FCSTD DOCUMENT  (FreeCAD 1.0R39109 (Git))
Label: TriggerAssembly
License: All rights reserved
LicenseURL: http://en.wikipedia.org/wiki/All_rights_reserved
objects: App::Link×5, App::FeaturePython×5, Assembly::JointGroup×1, Assembly::AssemblyObject×1
EXTERNAL_REF file=TriggerPivotBusing.stl.FCStd obj=Part
EXTERNAL_REF file=Trigger.stl.FCStd obj=Part001
EXTERNAL_REF file=../../ReferenceParts/M3.FCStd obj=Part

FEATURE [App::Link] Link014  label="TriggerPivotBushing"
  LinkPlacement = pos=(0,7e-16,3) rot=(-1,0,0;3.14159rad)
  LinkedObject = -> <external TriggerPivotBusing.stl.FCStd>#Part
  Placement = pos=(0,7e-16,3) rot=(-1,0,0;3.14159rad)
FEATURE [App::Link] Trigger_stl  label="Trigger.stl"
  LinkedObject = -> <external Trigger.stl.FCStd>#Part001
FEATURE [App::FeaturePython] GroundedJoint  # Assembly grounded joint (typed FeaturePython)
  ObjectToGround = -> Trigger_stl
FEATURE [App::FeaturePython] Joint  label="Fixed"  # Assembly joint (typed FeaturePython)
  Activated = true
  AngleMax = 0
  AngleMin = 0
  Detach1 = false
  Detach2 = false
  Distance = 0
  Distance2 = 0
  EnableAngleMax = false
  EnableAngleMin = false
  EnableLengthMax = false
  EnableLengthMin = false
  JointType = 0 (Fixed)
  LengthMax = 0
  LengthMin = 0
  Placement1 = pos=(0,3e-16,1.5) rot=(0,0,1;3.14159rad)
  Placement2 = pos=(0,3e-16,1.5) rot=(0,1,0;3.14159rad)
  Reference1 = -> Assembly [Link014.Body.Edge3,Link014.Body.Edge3]
  Reference2 = -> Assembly [Trigger_stl.Body.Edge63,Trigger_stl.Body.Edge63]
FEATURE [App::Link] M3x10  label="M3x011"
  LinkPlacement = pos=(-10.3581,0.779318,2.07e-14) rot=(0.970288,-0.171088,-0.171088;1.60095rad)
  LinkedObject = -> <external ../../ReferenceParts/M3.FCStd>#Part
  Placement = pos=(-10.3581,0.779318,2.07e-14) rot=(0.970288,-0.171088,-0.171088;1.60095rad)
FEATURE [App::Link] M3x011  label="M3x012"
  LinkPlacement = pos=(-18,2.55146,-6e-16) rot=(1,0,0;1.5708rad)
  LinkedObject = -> <external ../../ReferenceParts/M3.FCStd>#Part
  Placement = pos=(-18,2.55146,-6e-16) rot=(1,0,0;1.5708rad)
FEATURE [App::Link] M3x012  label="M3x013"
  LinkPlacement = pos=(25,-4,9e-16) rot=(1,0,0;1.5708rad)
  LinkedObject = -> <external ../../ReferenceParts/M3.FCStd>#Part
  Placement = pos=(25,-4,9e-16) rot=(1,0,0;1.5708rad)
FEATURE [App::FeaturePython] Joint002  label="Fixed002"  # Assembly joint (typed FeaturePython)
  Activated = true
  AngleMax = 0
  AngleMin = 0
  Detach1 = false
  Detach2 = false
  Distance = 0
  Distance2 = 0
  EnableAngleMax = false
  EnableAngleMin = false
  EnableLengthMax = false
  EnableLengthMin = false
  JointType = 0 (Fixed)
  LengthMax = 0
  LengthMin = 0
  Offset2 = pos=(0,0,6) rot=(0,0,1;0rad)
  Placement2 = pos=(-10.3581,0.779318,2.07e-14) rot=(0.970288,-0.171088,-0.171088;1.60095rad)
  Reference1 = -> Assembly [M3x10.Screw.Edge30,M3x10.Screw.Edge30]
  Reference2 = -> Assembly [Trigger_stl.Body.Edge30,Trigger_stl.Body.Edge30]
FEATURE [App::FeaturePython] Joint003  label="Fixed003"  # Assembly joint (typed FeaturePython)
  Activated = true
  AngleMax = 0
  AngleMin = 0
  Detach1 = false
  Detach2 = false
  Distance = 0
  Distance2 = 0
  EnableAngleMax = false
  EnableAngleMin = false
  EnableLengthMax = false
  EnableLengthMin = false
  JointType = 0 (Fixed)
  LengthMax = 0
  LengthMin = 0
  Offset2 = pos=(0,0,6) rot=(0,0,1;0rad)
  Placement2 = pos=(-18,2.55146,-6e-16) rot=(1,0,0;1.5708rad)
  Reference1 = -> Assembly [M3x011.Screw.Edge30,M3x011.Screw.Edge30]
  Reference2 = -> Assembly [Trigger_stl.Body.Edge5,Trigger_stl.Body.Edge5]
FEATURE [App::FeaturePython] Joint004  label="Fixed004"  # Assembly joint (typed FeaturePython)
  Activated = true
  AngleMax = 0
  AngleMin = 0
  Detach1 = false
  Detach2 = false
  Distance = 0
  Distance2 = 0
  EnableAngleMax = false
  EnableAngleMin = false
  EnableLengthMax = false
  EnableLengthMin = false
  JointType = 0 (Fixed)
  LengthMax = 0
  LengthMin = 0
  Offset2 = pos=(0,0,6) rot=(0,0,1;0rad)
  Placement2 = pos=(25,-4,9e-16) rot=(1,0,0;1.5708rad)
  Reference1 = -> Assembly [M3x012.Screw.Edge30,M3x012.Screw.Edge30]
  Reference2 = -> Assembly [Trigger_stl.Body.Edge40,Trigger_stl.Body.Edge40]
FEATURE [Assembly::JointGroup] Joints
  Group = -> [GroundedJoint,Joint,Joint002,Joint003,Joint004]
FEATURE [Assembly::AssemblyObject] Assembly  label="TriggerAssembly"
  Group = -> [Joints,Link014,Trigger_stl,GroundedJoint,Joint,M3x10,M3x011,M3x012,Joint002,Joint003,Joint004]
  Origin = -> Origin007
  Type = Assembly

RESOLVED EXTERNAL PARTS (link-assembly join: the EXTERNAL_REF files above that resolve inside this repo's crawl, each included once):
---- part Trigger.stl.FCStd = doc fcstd_24fa011b4839 ----
FCSTD DOCUMENT  (FreeCAD 1.0R39109 (Git))
Label: Trigger.stl
License: All rights reserved
LicenseURL: http://en.wikipedia.org/wiki/All_rights_reserved
objects: Sketcher::SketchObject×5, PartDesign::Pad×2, PartDesign::Pocket×2, PartDesign::Groove×1, PartDesign::Body×1, App::Part×1
note: 26 computed .brp shape members not serialized (recipe doc carries the construction recipe); baked Part::Feature solids carry a one-line shape summary decoded from their .brp

FEATURE [Sketcher::SketchObject] Sketch
  ArcFitTolerance = 1e-06
  AttachmentSupport = -> [XY_Plane002]
  FullyConstrained = true
  MakeInternals = false
  MapMode = 5
  sketch-geometry (17):
    g0: Circle [constr] CenterX=0 CenterY=0 CenterZ=0 NormalX=0 NormalY=0 NormalZ=1 AngleXU=0 Radius=6
    g1: LineSegment [constr] StartX=-5.63816 StartY=2.05212 StartZ=0 EndX=-18 EndY=6.55146 EndZ=0
    g2: LineSegment StartX=5.65685 StartY=2 StartZ=0 EndX=29 EndY=2 EndZ=0
    g3: LineSegment StartX=29 StartY=-2 StartZ=0 EndX=5.65685 EndY=-2 EndZ=0
    g4: LineSegment [constr] StartX=6 StartY=4.5e-15 StartZ=0 EndX=25 EndY=0 EndZ=0
    g5: ArcOfCircle CenterX=0 CenterY=0 CenterZ=0 NormalX=0 NormalY=0 NormalZ=1 AngleXU=0 Radius=6 StartAngle=0.339837 EndAngle=2.23203
    g6: ArcOfCircle CenterX=0 CenterY=0 CenterZ=0 NormalX=0 NormalY=0 NormalZ=1 AngleXU=0 Radius=6 StartAngle=2.928 EndAngle=5.94335
    g7: LineSegment [constr] StartX=-8.90908 StartY=6.63697 StartZ=0 EndX=-10.2772 EndY=2.8782 EndZ=0
    g8: LineSegment [constr] StartX=-18 StartY=8.55146 StartZ=0 EndX=-18 EndY=4.55146 EndZ=0
    g9: GeomPoint [constr] X=-10 Y=3.6397 Z=0
    g10: LineSegment StartX=-23 StartY=4.55146 StartZ=0 EndX=-14 EndY=4.55146 EndZ=0
    g11: LineSegment StartX=-14 StartY=4.55146 StartZ=0 EndX=-14 EndY=4.23321 EndZ=0
    g12: LineSegment StartX=-14 StartY=4.23321 StartZ=0 EndX=-5.86366 EndY=1.27182 EndZ=0
    g13: LineSegment StartX=-21.8309 StartY=8.55146 StartZ=0 EndX=-14.1691 EndY=8.55146 EndZ=0
    g14: LineSegment StartX=-14.1691 StartY=8.55146 StartZ=0 EndX=-3.68456 EndY=4.7354 EndZ=0
    g15: ArcOfCircle CenterX=0 CenterY=0 CenterZ=0 NormalX=0 NormalY=0 NormalZ=1 AngleXU=0 Radius=23.446 StartAngle=2.76825 EndAngle=2.94623
    g16: ArcOfCircle CenterX=0 CenterY=0 CenterZ=0 NormalX=0 NormalY=0 NormalZ=1 AngleXU=0 Radius=29.0689 StartAngle=6.21433 EndAngle=6.35204
  constraints (51):
    c: Coincident(g0,g-1)
    c: Diameter(g0) = 12
    c: PointOnObject(g5,g0)
    c: PointOnObject(g6,g0)
    c: PointOnObject(g1,g0)
    c: PointOnObject(g0,g1)
    c: Angle(g1,g-1) = 0.349066
    c: Horizontal(g2)
    c: Horizontal(g3)
    c: PointOnObject(g4,g0)
    c: PointOnObject(g4,g-1)
    c: Symmetric(g3,g2,g4)
    c: Coincident(g5,g0)
    c: Coincident(g5,g2)
    c: Coincident(g6,g3)
    c: Coincident(g6,g0)
    c: DistanceX(g-1,g4) = 25
    c: Symmetric(g8,g8,g1)
    c: Vertical(g8)
    c: Equal(g7,g8)
    c: DistanceY(g8,g8) = 4
    c: PointOnObject(g9,g1)
    c: DistanceX(g1,g-1) = 18
    c: DistanceX(g9,g-1) = 10
    c: Horizontal(g10)
    c: Coincident(g11,g10)
    c: Coincident(g12,g11)
    c: Coincident(g12,g6)
    c: PointOnObject(g7,g12)
    c: Vertical(g11)
    c: PointOnObject(g8,g10)
    c: DistanceX(g10,g8) = 5
    c: Horizontal(g13)
    c: Symmetric(g13,g13,g8)
    c: Coincident(g14,g13)
    c: Parallel(g14,g1)
    c: Perpendicular(g7,g12)
    c: Coincident(g14,g5)
    c: Perpendicular(g1,g7)
    c: PointOnObject(g9,g7)
    c: DistanceX(g8,g10) = 4
    c: PointOnObject(g7,g14)
    c: Coincident(g15,g0)
    c: Coincident(g15,g13)
    c: Coincident(g15,g10)
    c: Distance(g13,g-1) = 23.446
    c: Distance(g2,g3) = 4
    c: Coincident(g16,g0)
    c: Coincident(g16,g2)
    c: Coincident(g16,g3)
    c: DistanceX(g4,g2) = 4
FEATURE [PartDesign::Pad] Pad
  Direction = (0,0,1)
  Length = 8
  Length2 = 10
  Midplane = true
  Profile = -> Sketch
  ReferenceAxis = -> Sketch [N_Axis]
  Refine = true
  Suppressed = false
  Type = 0
FEATURE [Sketcher::SketchObject] Sketch001
  ArcFitTolerance = 1e-06
  AttachmentOffset = pos=(0,0,0) rot=(0,0,1;-0.174533rad)
  AttachmentSupport = -> [XY_Plane002]
  FullyConstrained = true
  MakeInternals = false
  MapMode = 5
  Placement = pos=(0,0,0) rot=(0,0,1;6.10865rad)
  sketch-geometry (9):
    g0: ArcOfCircle CenterX=58 CenterY=-24 CenterZ=0 NormalX=0 NormalY=0 NormalZ=1 AngleXU=0 Radius=59 StartAngle=2.82598 EndAngle=3.32291
    g1: ArcOfCircle CenterX=-2 CenterY=-35 CenterZ=0 NormalX=0 NormalY=0 NormalZ=1 AngleXU=0 Radius=2 StartAngle=3.38066 EndAngle=6.46451
    g2: ArcOfCircle CenterX=87.924 CenterY=-13.0833 CenterZ=0 NormalX=0 NormalY=0 NormalZ=1 AngleXU=0 Radius=94.5563 StartAngle=3.01546 EndAngle=3.38066
    g3: GeomPoint X=0 Y=-35 Z=0
    g4: Circle [constr] CenterX=0 CenterY=0 CenterZ=0 NormalX=0 NormalY=0 NormalZ=1 AngleXU=0 Radius=6
    g5: ArcOfCircle CenterX=0 CenterY=0 CenterZ=0 NormalX=0 NormalY=0 NormalZ=1 AngleXU=0 Radius=6 StartAngle=3.34098 EndAngle=5.0371
    g6: GeomPoint X=-1 Y=-24 Z=0
    g7: GeomPoint X=0 Y=-24 Z=0
    g8: GeomPoint X=-6 Y=-24 Z=0
  constraints (23):
    c: Tangent(g2,g1) = -1.5708
    c: Tangent(g1,g0) = 1.5708
    c: PointOnObject(g3,g1)
    c: Horizontal(g3,g1)
    c: DistanceY(g3,g-1) = 35
    c: Radius(g1) = 2
    c: Coincident(g4,g-1)
    c: Diameter(g4) = 12
    c: Coincident(g5,g4)
    c: Coincident(g5,g0)
    c: Coincident(g5,g2)
    c: PointOnObject(g3,g-2)
    c: PointOnObject(g0,g4)
    c: PointOnObject(g6,g0)
    c: PointOnObject(g7,g-2)
    c: Horizontal(g7,g6)
    c: DistanceX(g6,g7) = 1
    c: Horizontal(g0,g7)
    c: PointOnObject(g8,g2)
    c: Horizontal(g8,g6)
    c: DistanceX(g8,g6) = 5
    c: Distance(g2,g0) = 9
    c: DistanceY(g7,g-1) = 24
FEATURE [PartDesign::Pad] Pad001
  BaseFeature = -> Pad
  Direction = (0,0,1)
  Length = 8
  Length2 = 10
  Midplane = true
  Profile = -> Sketch001
  ReferenceAxis = -> Sketch001 [N_Axis]
  Refine = true
  Suppressed = false
  Type = 0
FEATURE [Sketcher::SketchObject] Sketch002
  ArcFitTolerance = 1e-06
  AttachmentSupport = -> [XZ_Plane002]
  FullyConstrained = true
  MakeInternals = false
  MapMode = 5
  Placement = pos=(0,0,0) rot=(1,0,0;1.5708rad)
  sketch-geometry (6):
    g0: LineSegment StartX=0 StartY=-20 StartZ=0 EndX=-4.1 EndY=-20 EndZ=0
    g1: LineSegment StartX=-4.1 StartY=-20 StartZ=0 EndX=-4.1 EndY=1.5 EndZ=0
    g2: LineSegment StartX=-4.1 StartY=1.5 StartZ=0 EndX=-6 EndY=1.5 EndZ=0
    g3: LineSegment StartX=-6 StartY=1.5 StartZ=0 EndX=-24.5 EndY=20 EndZ=0
    g4: LineSegment StartX=-24.5 StartY=20 StartZ=0 EndX=0 EndY=20 EndZ=0
    g5: LineSegment StartX=0 StartY=20 StartZ=0 EndX=0 EndY=-20 EndZ=0
  constraints (18):
    c: PointOnObject(g0,g-2)
    c: Horizontal(g0)
    c: Coincident(g0,g1)
    c: Vertical(g1)
    c: Coincident(g1,g2)
    c: Horizontal(g2)
    c: Coincident(g2,g3)
    c: Coincident(g3,g4)
    c: Horizontal(g4)
    c: Coincident(g4,g5)
    c: Coincident(g5,g0)
    c: Vertical(g5)
    c: DistanceY(g0,g-1) = 20
    c: DistanceX(g0,g-1) = 4.1
    c: DistanceX(g2,g-1) = 6
    c: DistanceY(g-1,g1) = 1.5
    c: Angle(g2,g3) = 2.35619
    c: DistanceY(g-1,g4) = 20
FEATURE [PartDesign::Groove] Groove
  Angle = 360
  Angle2 = 60
  Axis = (0,2e-16,1)
  Base = (0,0,0)
  BaseFeature = -> Pad001
  Profile = -> Sketch002
  ReferenceAxis = -> Sketch002 [V_Axis]
  Refine = true
  Reversed = true
  Suppressed = false
  Type = 0
FEATURE [Sketcher::SketchObject] Sketch003
  ArcFitTolerance = 1e-06
  AttachmentSupport = -> [XZ_Plane002]
  FullyConstrained = true
  MakeInternals = false
  MapMode = 5
  Placement = pos=(0,0,0) rot=(1,0,0;1.5708rad)
  sketch-geometry (2):
    g0: Circle CenterX=25 CenterY=0 CenterZ=0 NormalX=0 NormalY=0 NormalZ=1 AngleXU=0 Radius=1.25
    g1: Circle CenterX=-18 CenterY=0 CenterZ=0 NormalX=0 NormalY=0 NormalZ=1 AngleXU=0 Radius=1.25
  constraints (6):
    c: PointOnObject(g0,g-1)
    c: PointOnObject(g1,g-1)
    c: DistanceX(g1,g-1) = 18
    c: DistanceX(g-1,g0) = 25
    c: Equal(g0,g1)
    c: Diameter(g1) = 2.5
FEATURE [PartDesign::Pocket] Pocket  label="BoltHoles1"
  BaseFeature = -> Groove
  Direction = (0,1,-2e-16)
  Length = 5
  Length2 = 5
  Midplane = true
  Profile = -> Sketch003
  ReferenceAxis = -> Sketch003 [N_Axis]
  Refine = true
  Suppressed = false
  Type = 1
FEATURE [Sketcher::SketchObject] Sketch004
  ArcFitTolerance = 1e-06
  AttachmentOffset = pos=(0,0,0) rot=(0,-1,0;0.349066rad)
  AttachmentSupport = -> [XZ_Plane002]
  FullyConstrained = true
  MakeInternals = false
  MapMode = 5
  Placement = pos=(0,0,0) rot=(0.970288,-0.171088,-0.171088;1.60095rad)
  sketch-geometry (1):
    g0: Circle CenterX=-10 CenterY=0 CenterZ=0 NormalX=0 NormalY=0 NormalZ=1 AngleXU=0 Radius=1.25
  constraints (3):
    c: PointOnObject(g0,g-1)
    c: DistanceX(g0,g-1) = 10
    c: Diameter(g0) = 2.5
FEATURE [PartDesign::Pocket] Pocket001
  BaseFeature = -> Pocket
  Direction = (0.34202,0.939693,-1e-16)
  Length = 5
  Length2 = 5
  Midplane = true
  Profile = -> Sketch004
  ReferenceAxis = -> Sketch004 [N_Axis]
  Refine = true
  Suppressed = false
  Type = 1
FEATURE [PartDesign::Body] Body
  AllowCompound = false
  Group = -> [Sketch,Pad,Sketch001,Pad001,Sketch002,Groove,Sketch003,Pocket,Sketch004,Pocket001]
  Origin = -> Origin002
  Tip = -> Pocket001
FEATURE [App::Part] Part001  label="Trigger.stl"
  Group = -> [Body]
  Origin = -> Origin001
---- part TriggerPivotBusing.stl.FCStd = doc fcstd_a534dfd0ede6 ----
FCSTD DOCUMENT  (FreeCAD 1.0R39109 (Git))
Label: TriggerPivotBusing.stl
License: All rights reserved
LicenseURL: http://en.wikipedia.org/wiki/All_rights_reserved
objects: Sketcher::SketchObject×1, PartDesign::Revolution×1, PartDesign::Chamfer×1, PartDesign::Body×1, App::Part×1
note: 9 computed .brp shape members not serialized (recipe doc carries the construction recipe); baked Part::Feature solids carry a one-line shape summary decoded from their .brp

FEATURE [Sketcher::SketchObject] Sketch
  ArcFitTolerance = 1e-06
  AttachmentSupport = -> [XZ_Plane]
  FullyConstrained = true
  MakeInternals = false
  MapMode = 5
  Placement = pos=(0,0,0) rot=(1,0,0;1.5708rad)
  sketch-geometry (9):
    g0: LineSegment StartX=-1.6 StartY=0 StartZ=0 EndX=-6 EndY=0 EndZ=0
    g1: LineSegment StartX=-6 StartY=0 StartZ=0 EndX=-6 EndY=1 EndZ=0
    g2: LineSegment StartX=-5 StartY=1.5 StartZ=0 EndX=-4 EndY=1.5 EndZ=0
    g3: LineSegment StartX=-4 StartY=1.5 StartZ=0 EndX=-4 EndY=7.2 EndZ=0
    g4: LineSegment StartX=-4 StartY=7.2 StartZ=0 EndX=-1.6 EndY=7.2 EndZ=0
    g5: LineSegment StartX=-1.6 StartY=7.2 StartZ=0 EndX=-1.6 EndY=0 EndZ=0
    g6: GeomPoint [constr] X=-6 Y=1.5 Z=0
    g7: LineSegment StartX=-6 StartY=1 StartZ=0 EndX=-5 EndY=1 EndZ=0
    g8: LineSegment StartX=-5 StartY=1.5 StartZ=0 EndX=-5 EndY=1 EndZ=0
  constraints (26):
    c: PointOnObject(g0,g-1)
    c: PointOnObject(g0,g-1)
    c: Coincident(g0,g1)
    c: Vertical(g1)
    c: Horizontal(g2)
    c: Coincident(g2,g3)
    c: Vertical(g3)
    c: Coincident(g3,g4)
    c: Horizontal(g4)
    c: Coincident(g4,g5)
    c: Coincident(g5,g0)
    c: Vertical(g5)
    c: DistanceX(g0,g-1) = 1.6
    c: DistanceX(g3,g-1) = 4
    c: DistanceX(g6,g2) = 2
    c: DistanceY(g1,g6) = 1.5
    c: DistanceY(g-1,g4) = 7.2
    c: PointOnObject(g6,g1)
    c: PointOnObject(g6,g2)
    c: Coincident(g1,g7)
    c: Horizontal(g7)
    c: Coincident(g2,g8)
    c: Coincident(g8,g7)
    c: Vertical(g8)
    c: DistanceY(g8,g8) = 0.5
    c: DistanceX(g2,g2) = 1
FEATURE [PartDesign::Revolution] Revolution
  Angle = 360
  Angle2 = 60
  Axis = (0,2e-16,1)
  Base = (0,0,0)
  Placement = pos=(0,0,0) rot=(1,0,0;1.5708rad)
  Profile = -> Sketch
  ReferenceAxis = -> Sketch [V_Axis]
  Refine = true
  Suppressed = false
  Type = 0
FEATURE [PartDesign::Chamfer] Chamfer
  Angle = 45
  Base = -> Revolution [Face5,Face3]
  BaseFeature = -> Revolution
  ChamferType = 0
  FlipDirection = false
  Placement = pos=(0,0,0) rot=(1,0,0;1.5708rad)
  Refine = true
  Size = 0.25
  Size2 = 1
  SupportTransform = false
  Suppressed = false
  UseAllEdges = false
FEATURE [PartDesign::Body] Body
  AllowCompound = false
  Group = -> [Sketch,Revolution,Chamfer]
  Origin = -> Origin
  Tip = -> Chamfer
FEATURE [App::Part] Part  label="TriggerPivotBushing.stl"
  Group = -> [Body]
  Origin = -> Origin001
